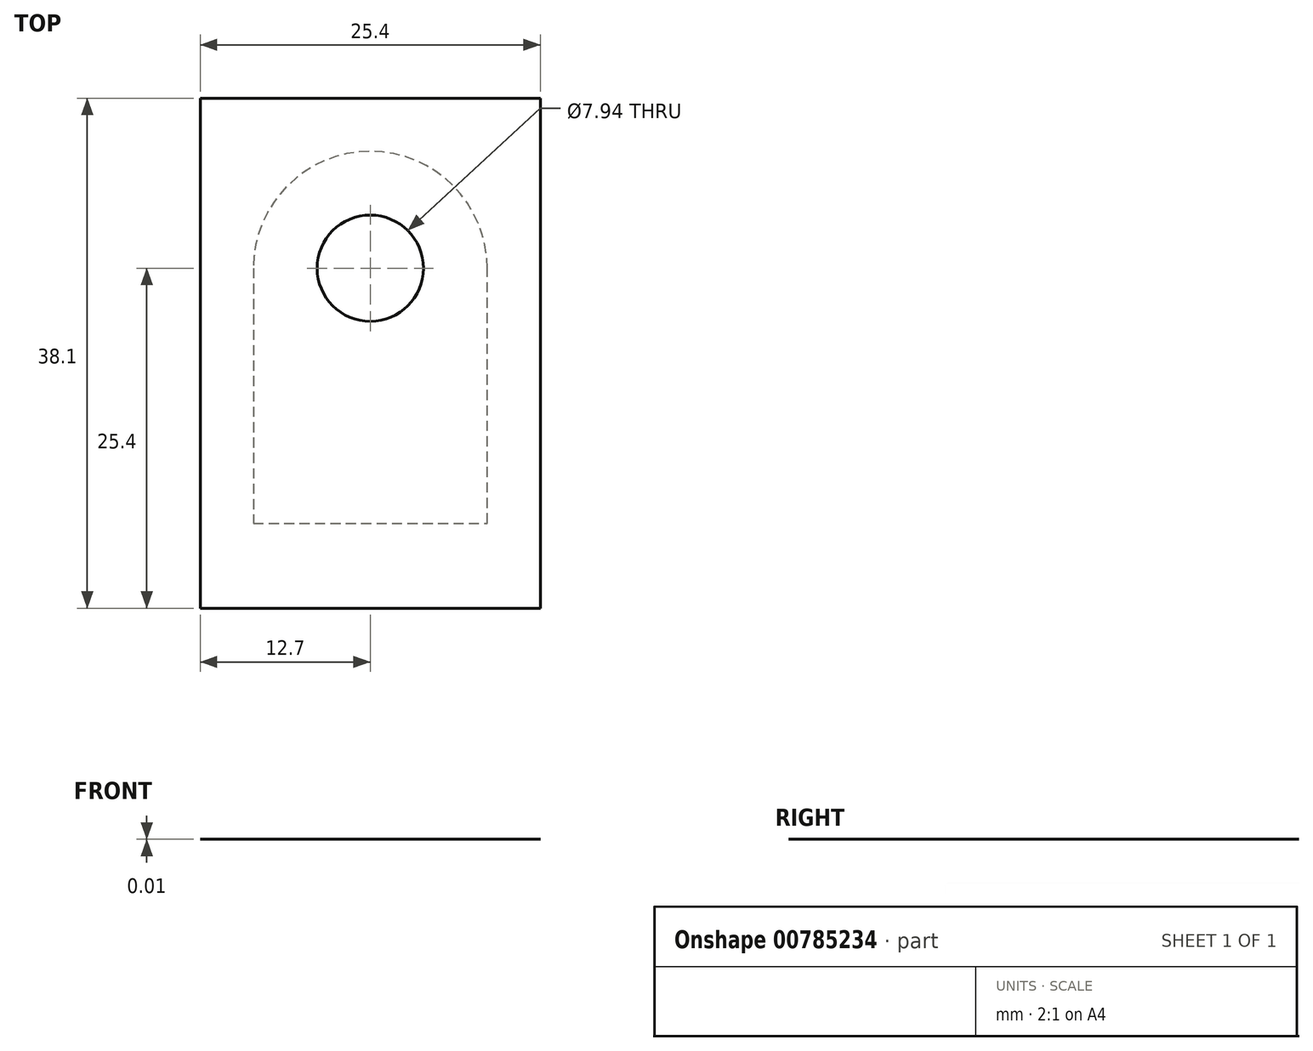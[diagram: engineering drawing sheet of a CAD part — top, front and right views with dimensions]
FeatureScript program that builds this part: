
annotation { "Feature Type Name" : "Feature", "Feature Type Description" : "" }
export const myFeature = defineFeature(function(context is Context, id is Id, definition is map)
    precondition{}
    {
        {
            var Q0;
            Q0=qCreatedBy(makeId("Top.planeOp"),FACE);
            var sketch = newSketch(context, id + "F0", { "sketchPlane" : qUnion([Q0])});
            skLineSegment(sketch, "E0.top", {"start": v(12.7, -25.4) * mm, "end": v(-12.7, -25.4) * mm});
            skPoint(sketch, "E0.middle", {"position": v(0, 0) * mm});
            skCircle(sketch, "E1", {"center": v(0, 0) * mm, "radius": 8.73 * mm});
            skLineSegment(sketch, "E2", {"start": v(-8.73, 0) * mm, "end": v(-8.73, -19.05) * mm});
            skLineSegment(sketch, "E3.bottom", {"start": v(-8.73, -19.05) * mm, "end": v(8.73, -19.05) * mm});
            skLineSegment(sketch, "E3.left", {"start": v(-8.73, -19.05) * mm, "end": v(-8.73, 0) * mm});
            skLineSegment(sketch, "E3.right", {"start": v(8.73, -19.05) * mm, "end": v(8.73, 0) * mm});
            skLineSegment(sketch, "E4", {"start": v(-12.7, 12.7) * mm, "end": v(12.7, 12.7) * mm});
            skLineSegment(sketch, "E5", {"start": v(12.7, 12.7) * mm, "end": v(12.7, -25.4) * mm});
            skLineSegment(sketch, "E6", {"start": v(-12.7, -25.4) * mm, "end": v(-12.7, 12.7) * mm});
            skSolve(sketch);
        }
        {
            var Q0;
            Q0=qSketchRegion(id+"F0",true);
            extrude(context, id + "F1", {"entities" : qUnion([Q0]), "depth" : 3 / 406.4 * mm, "offsetDistance" : 25.4 * mm});
        }
        {
            var Q0;
            Q0=makeQuery(id+"F1.opExtrude","CAP_FACE",FACE,{"disambiguationData":[OSD([sQuery(id+"F0.wireOp",EDGE,"E1"),sQuery(id+"F0.wireOp",EDGE,"E3.bottom"),sQuery(id+"F0.wireOp",EDGE,"E3.left"),sQuery(id+"F0.wireOp",EDGE,"E3.right"),sQuery(id+"F0.wireOp",EDGE,"E4"),sQuery(id+"F0.wireOp",EDGE,"E5"),sQuery(id+"F0.wireOp",EDGE,"E0.top"),sQuery(id+"F0.wireOp",EDGE,"E6")])],"isStart":false});
            var sketch = newSketch(context, id + "F2", { "sketchPlane" : qUnion([Q0])});
            skLineSegment(sketch, "E7.bottom", {"start": v(-12.7, 12.7) * mm, "end": v(12.7, 12.7) * mm});
            skLineSegment(sketch, "E7.top", {"start": v(-12.7, -25.4) * mm, "end": v(12.7, -25.4) * mm});
            skLineSegment(sketch, "E7.left", {"start": v(-12.7, 12.7) * mm, "end": v(-12.7, -25.4) * mm});
            skLineSegment(sketch, "E7.right", {"start": v(12.7, 12.7) * mm, "end": v(12.7, -25.4) * mm});
            skCircle(sketch, "E8", {"center": v(0, 0) * mm, "radius": 3.97 * mm});
            skSolve(sketch);
        }
        {
            var Q0;
            Q0=qSketchRegion(id+"F2",true);
            extrude(context, id + "F3", {"entities" : qUnion([Q0]), "operationType" : NewBodyOperationType.ADD, "depth" : 3 / 812.8 * mm, "offsetDistance" : 25.4 * mm});
        }
    });
